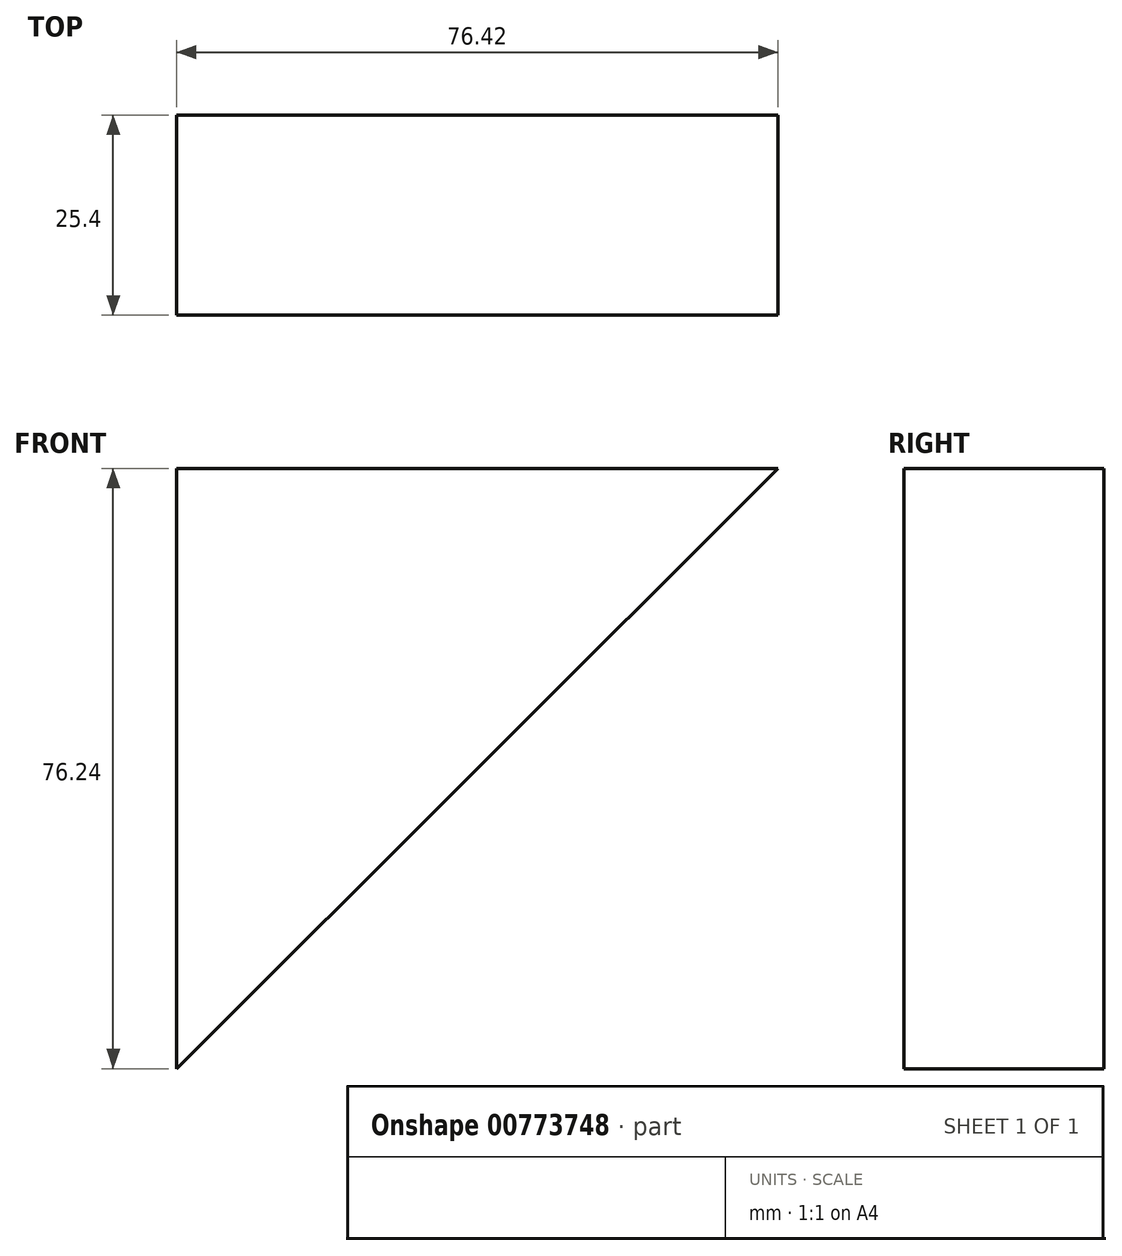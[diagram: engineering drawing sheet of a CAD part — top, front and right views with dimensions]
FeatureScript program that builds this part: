
annotation { "Feature Type Name" : "Feature", "Feature Type Description" : "" }
export const myFeature = defineFeature(function(context is Context, id is Id, definition is map)
    precondition{}
    {
        {
            var Q0;
            Q0=qCreatedBy(makeId("Front.planeOp"),FACE);
            var sketch = newSketch(context, id + "F0", { "sketchPlane" : qUnion([Q0])});
            skLineSegment(sketch, "E0", {"start": v(75.7, 75.51) * mm, "end": v(0, 0) * mm});
            skLineSegment(sketch, "E1", {"start": v(0, 0) * mm, "end": v(76.42, 0) * mm});
            skLineSegment(sketch, "E2", {"start": v(76.42, 0) * mm, "end": v(0, -76.24) * mm});
            skLineSegment(sketch, "E3", {"start": v(0, -76.24) * mm, "end": v(0, 0) * mm});
            skLineSegment(sketch, "E4", {"start": v(-74.5, 0) * mm, "end": v(0, 0) * mm});
            skLineSegment(sketch, "E5", {"start": v(0, 0) * mm, "end": v(0, 75.77) * mm});
            skSolve(sketch);
        }
        {
            var Q0;
            Q0 = qSketchRegion(id + "F0", true);
            extrude(context, id + "F1", {"entities" : qUnion([Q0]), "depth" : 25.4 * mm, "offsetDistance" : 25.4 * mm});
        }
    });
